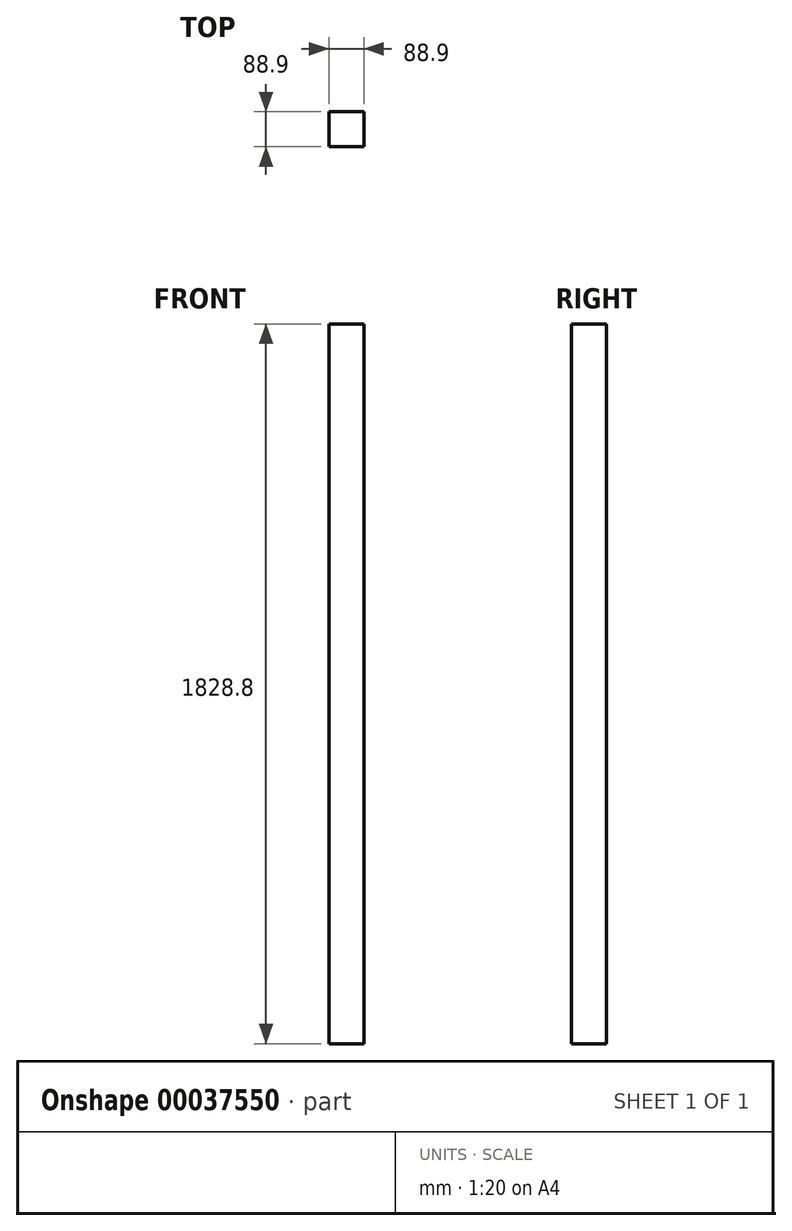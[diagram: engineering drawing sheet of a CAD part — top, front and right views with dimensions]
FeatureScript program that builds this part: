
annotation { "Feature Type Name" : "Feature", "Feature Type Description" : "" }
export const myFeature = defineFeature(function(context is Context, id is Id, definition is map)
    precondition{}
    {
        {
            var Q0;
            Q0=qCreatedBy(makeId("Top.planeOp"),FACE);
            var sketch = newSketch(context, id + "F0", { "sketchPlane" : qUnion([Q0])});
            skLineSegment(sketch, "E0.bottom", {"start": v(-44.45, 44.45) * mm, "end": v(44.45, 44.45) * mm});
            skLineSegment(sketch, "E0.top", {"start": v(-44.45, -44.45) * mm, "end": v(44.45, -44.45) * mm});
            skLineSegment(sketch, "E0.left", {"start": v(-44.45, 44.45) * mm, "end": v(-44.45, -44.45) * mm});
            skLineSegment(sketch, "E0.right", {"start": v(44.45, 44.45) * mm, "end": v(44.45, -44.45) * mm});
            skLineSegment(sketch, "E1", {"start": v(0, 0) * mm, "end": v(0, 44.45) * mm, "construction": true});
            skLineSegment(sketch, "E2", {"start": v(0, 0) * mm, "end": v(-44.45, 0) * mm, "construction": true});
            skSolve(sketch);
        }
        {
            var Q0;
            Q0 = qSketchRegion(id + "F0", true);
            extrude(context, id + "F1", {"entities" : qUnion([Q0]), "depth" : 1828.8 * mm});
        }
    });
